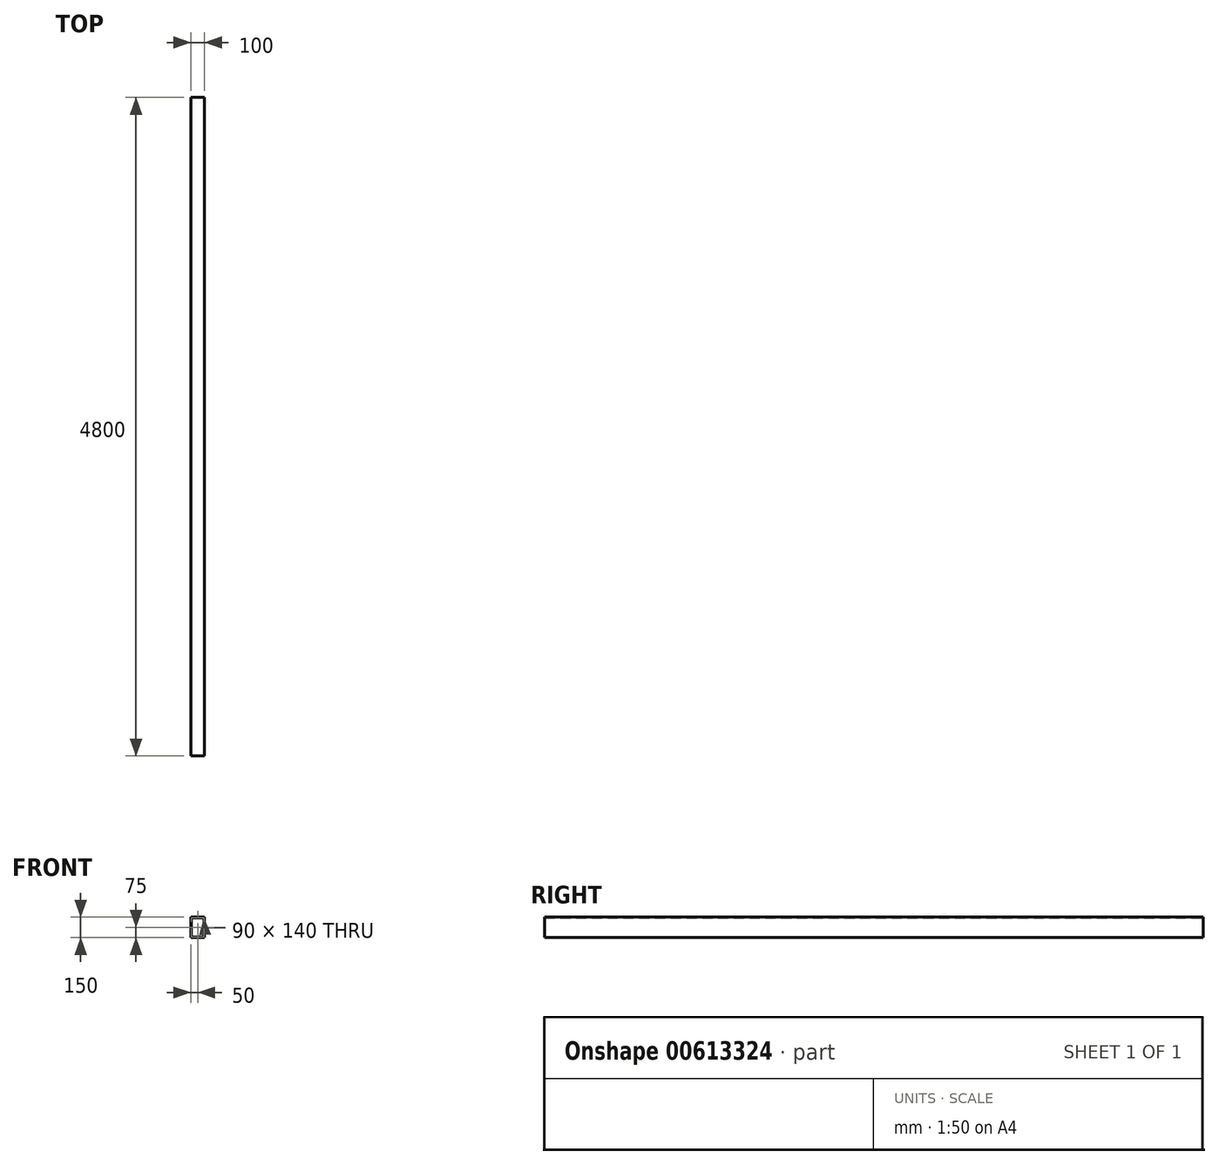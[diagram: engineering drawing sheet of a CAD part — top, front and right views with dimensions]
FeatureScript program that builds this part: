
annotation { "Feature Type Name" : "Feature", "Feature Type Description" : "" }
export const myFeature = defineFeature(function(context is Context, id is Id, definition is map)
    precondition{}
    {
        {
            var Q0;
            Q0=qCreatedBy(makeId("Front.planeOp"),FACE);
            var sketch = newSketch(context, id + "F0", { "sketchPlane" : qUnion([Q0])});
            skLineSegment(sketch, "E0.bottom", {"start": v(0, 0) * mm, "end": v(100, 0) * mm});
            skLineSegment(sketch, "E0.top", {"start": v(0, 150) * mm, "end": v(100, 150) * mm});
            skLineSegment(sketch, "E0.left", {"start": v(0, 0) * mm, "end": v(0, 150) * mm});
            skLineSegment(sketch, "E0.right", {"start": v(100, 0) * mm, "end": v(100, 150) * mm});
            skLineSegment(sketch, "E1.0", {"start": v(5, 145) * mm, "end": v(95, 145) * mm});
            skLineSegment(sketch, "E1.1", {"start": v(5, 5) * mm, "end": v(5, 145) * mm});
            skLineSegment(sketch, "E1.2", {"start": v(5, 5) * mm, "end": v(95, 5) * mm});
            skLineSegment(sketch, "E1.3", {"start": v(95, 5) * mm, "end": v(95, 145) * mm});
            skSolve(sketch);
        }
        {
            var Q0;
            Q0=makeQuery(id+"F0.imprint","IMPRINT",FACE,{"disambiguationData":[TD([[makeQuery(id+"F0.imprint","IMPRINT",EDGE,{"derivedFrom":sQuery(id+"F0.wireOp",EDGE,"E0.bottom")}),1.0]])]});
            extrude(context, id + "F1", {"entities" : qUnion([Q0]), "depth" : 4800 * mm, "offsetDistance" : 25 * mm});
        }
    });
